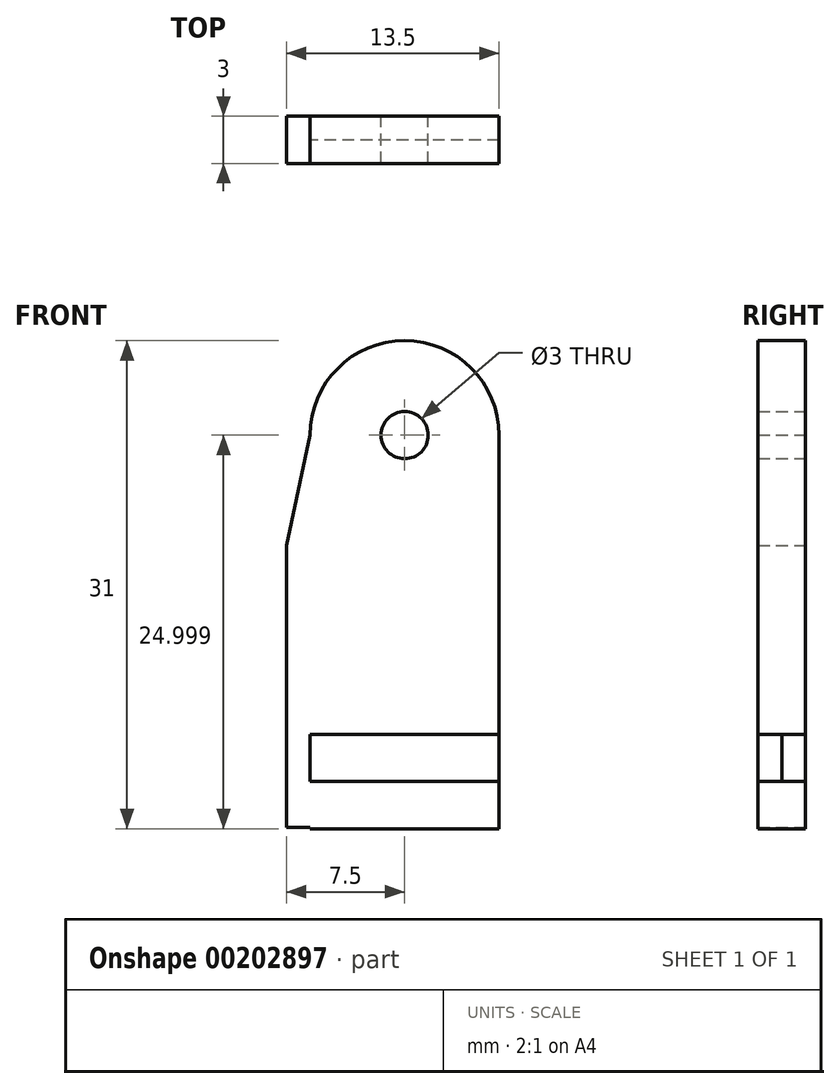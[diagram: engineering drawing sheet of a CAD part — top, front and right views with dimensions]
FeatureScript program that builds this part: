
annotation { "Feature Type Name" : "Feature", "Feature Type Description" : "" }
export const myFeature = defineFeature(function(context is Context, id is Id, definition is map)
    precondition{}
    {
        {
            var Q0;
            Q0=qCreatedBy(makeId("Front.planeOp"),FACE);
            var sketch = newSketch(context, id + "F0", { "sketchPlane" : qUnion([Q0])});
            skLineSegment(sketch, "E0", {"start": v(-49.52, 0) * mm, "end": v(53.2, 0) * mm, "construction": true});
            skLineSegment(sketch, "E1", {"start": v(0, 54.81) * mm, "end": v(0, -48.53) * mm, "construction": true});
            skLineSegment(sketch, "E2", {"start": v(-6, -6.27) * mm, "end": v(-6, -9.27) * mm});
            skLineSegment(sketch, "E3", {"start": v(-6, -12.27) * mm, "end": v(0, -12.27) * mm});
            skLineSegment(sketch, "E4", {"start": v(-6, -9.27) * mm, "end": v(0, -9.27) * mm});
            skLineSegment(sketch, "E5", {"start": v(-6, -6.27) * mm, "end": v(0, -6.27) * mm});
            skLineSegment(sketch, "E6.MirrorCS", {"start": v(6, 0) * mm, "end": v(6, 12.73) * mm});
            skLineSegment(sketch, "E7.MirrorCS", {"start": v(6, 0) * mm, "end": v(6, -12.27) * mm});
            skLineSegment(sketch, "E8.MirrorCS", {"start": v(6, -6.27) * mm, "end": v(0, -6.27) * mm});
            skLineSegment(sketch, "E9.MirrorCS", {"start": v(6, -9.27) * mm, "end": v(0, -9.27) * mm});
            skLineSegment(sketch, "E10.MirrorCS", {"start": v(6, -12.27) * mm, "end": v(0, -12.27) * mm});
            skArc(sketch, "E11", {"start": v(6, 12.73) * mm, "mid": v(0, 18.73) * mm, "end": v(-6, 12.73) * mm});
            skCircle(sketch, "E12", {"center": v(0, 32.21) * mm, "radius": 1.5 * mm});
            skLineSegment(sketch, "E13", {"start": v(-7.38, 12.73) * mm, "end": v(9.04, 12.73) * mm, "construction": true});
            skCircle(sketch, "E14", {"center": v(0, 12.73) * mm, "radius": 1.5 * mm});
            skLineSegment(sketch, "E15.top", {"start": v(-6, -12.2) * mm, "end": v(-7.5, -12.2) * mm});
            skLineSegment(sketch, "E15.right", {"start": v(-7.5, -6.27) * mm, "end": v(-7.5, -12.2) * mm});
            skLineSegment(sketch, "E16.trimOffspring", {"start": v(-6, -12.2) * mm, "end": v(-6, -12.27) * mm});
            skLineSegment(sketch, "E17", {"start": v(-9.07, 5.73) * mm, "end": v(8.9, 5.73) * mm, "construction": true});
            skPoint(sketch, "E18.end.orphan", {"position": v(-6, 0) * mm});
            skLineSegment(sketch, "E19", {"start": v(-7.5, -6.27) * mm, "end": v(-7.5, 5.73) * mm});
            skLineSegment(sketch, "E20", {"start": v(-7.5, 5.73) * mm, "end": v(-6, 12.73) * mm});
            skSolve(sketch);
        }
        {
            var Q0;
            {var subQ3=sQuery(id+"F0.wireOp",EDGE,"E3");Q0=makeQuery(id+"F0.imprint","IMPRINT",FACE,{"disambiguationData":[TD([[makeQuery(id+"F0.imprint","IMPRINT",EDGE,{"derivedFrom":subQ3}),1.0]])]});}
            var Q1;
            {var subQ2=sQuery(id+"F0.wireOp",EDGE,"E5");Q1=makeQuery(id+"F0.imprint","IMPRINT",FACE,{"disambiguationData":[TD([[makeQuery(id+"F0.imprint","IMPRINT",EDGE,{"derivedFrom":subQ2}),1.0]])]});}
            extrude(context, id + "F1", {"entities" : qUnion([Q0, Q1]), "depth" : 3 * mm});
        }
        {
            var Q0;
            {var subQ4=sQuery(id+"F0.wireOp",EDGE,"E4");Q0=makeQuery(id+"F0.imprint","IMPRINT",FACE,{"disambiguationData":[TD([[makeQuery(id+"F0.imprint","IMPRINT",EDGE,{"derivedFrom":subQ4}),1.0]])]});}
            extrude(context, id + "F2", {"entities" : qUnion([Q0]), "depth" : 1.5 * mm});
        }
    });
